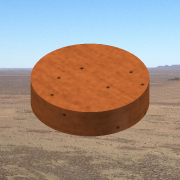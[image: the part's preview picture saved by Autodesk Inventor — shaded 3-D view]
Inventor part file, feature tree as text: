
AUTODESK INVENTOR PART (.ipt)
format: ipt  version: 2014 SP1 (Build 180222100, 222)  size: 125,952 bytes
history: native  units: in
note: dims shown in document units (in); Inventor stores cm internally (conversion verified against a paired STEP export)
features: extrude x1, sketch x1
ambient origin geometry x8: Origin, YZ Plane, XZ Plane, XY Plane, X Axis, Y Axis, Z Axis, Center Point
bodies: Solid1 (feature_tree)
feature tree (2):
  extrude  "Extrusion1"  Depth=0.5in TaperAngle=0.0deg
  sketch  "Sketch1"  dims[d0=2.0in d1=0.5in d2=0.0in]
